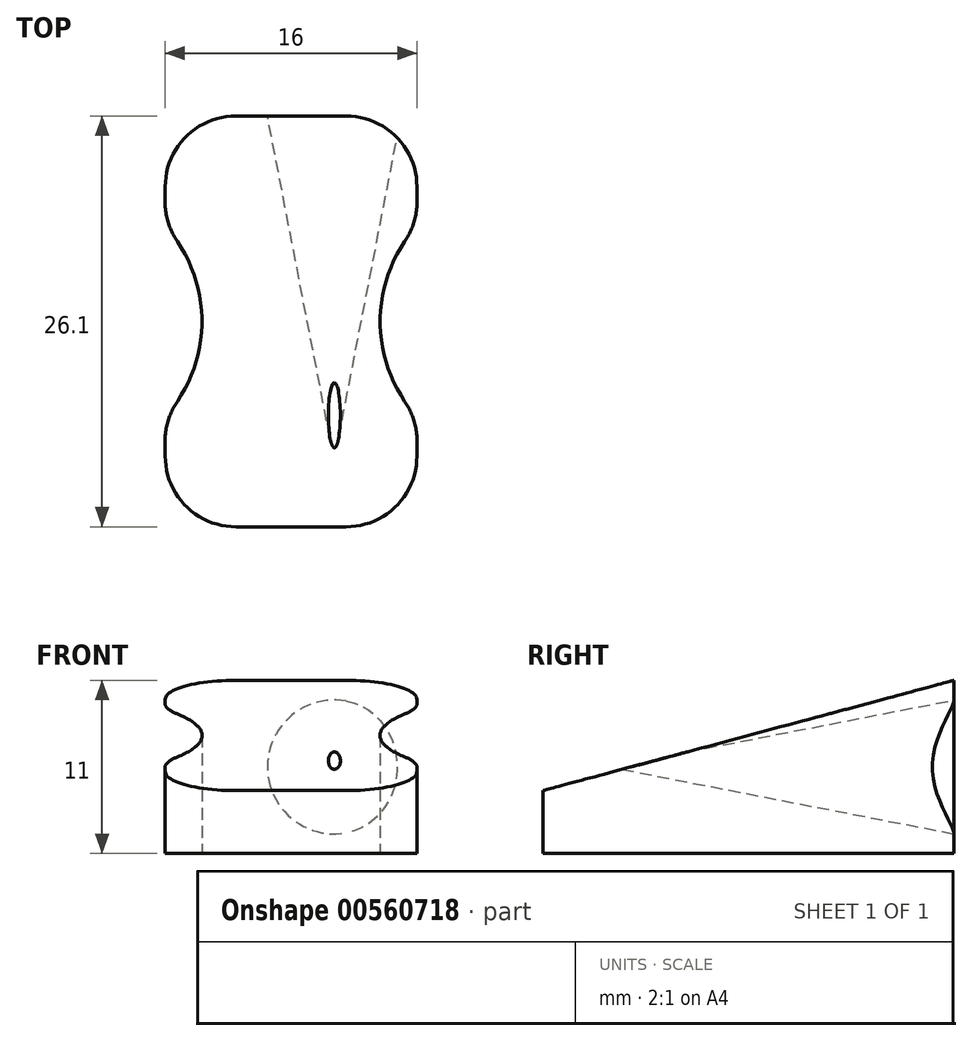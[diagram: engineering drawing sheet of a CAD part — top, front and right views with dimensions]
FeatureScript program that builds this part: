
annotation { "Feature Type Name" : "Feature", "Feature Type Description" : "" }
export const myFeature = defineFeature(function(context is Context, id is Id, definition is map)
    precondition{}
    {
        {
            var Q0;
            Q0=qCreatedBy(makeId("Top.planeOp"),FACE);
            var sketch = newSketch(context, id + "F0", { "sketchPlane" : qUnion([Q0])});
            skLineSegment(sketch, "E0.bottom", {"start": v(-8, 26.1) * mm, "end": v(8, 26.1) * mm});
            skLineSegment(sketch, "E0.top", {"start": v(-8, 0) * mm, "end": v(8, 0) * mm});
            skLineSegment(sketch, "E0.left", {"start": v(-8, 26.1) * mm, "end": v(-8, 0) * mm});
            skLineSegment(sketch, "E0.right", {"start": v(8, 26.1) * mm, "end": v(8, 0) * mm});
            skSolve(sketch);
        }
        {
            var Q0;
            Q0 = qSketchRegion(id + "F0", true);
            extrude(context, id + "F1", {"entities" : qUnion([Q0]), "depth" : 11 * mm, "offsetDistance" : 25 * mm});
        }
        {
            var Q0;
            Q0=qCreatedBy(makeId("Top.planeOp"),FACE);
            var sketch = newSketch(context, id + "F2", { "sketchPlane" : qUnion([Q0])});
            skLineSegment(sketch, "E1", {"start": v(0, 26.1) * mm, "end": v(0, 0) * mm, "construction": true});
            skLineSegment(sketch, "E2", {"start": v(0, 13.05) * mm, "end": v(-14.65, 13.05) * mm, "construction": true});
            skPoint(sketch, "E2.endSnap0", {"position": v(0, 13.05) * mm});
            skCircle(sketch, "E3", {"center": v(-14.65, 13.05) * mm, "radius": 9 * mm});
            skCircle(sketch, "E4.MirrorC", {"center": v(14.65, 13.05) * mm, "radius": 9 * mm});
            skSolve(sketch);
        }
        {
            var Q0;
            Q0 = qSketchRegion(id + "F2", true);
            extrude(context, id + "F3", {"entities" : qUnion([Q0]), "operationType" : NewBodyOperationType.REMOVE, "depth" : 25 * mm, "offsetDistance" : 25 * mm});
        }
        {
            var Q0;
            Q0=qCreatedBy(makeId("Right.planeOp"),FACE);
            var sketch = newSketch(context, id + "F4", { "sketchPlane" : qUnion([Q0])});
            skLineSegment(sketch, "E5", {"start": v(26.1, 11) * mm, "end": v(0, 4) * mm});
            skLineSegment(sketch, "E6", {"start": v(26.1, 11) * mm, "end": v(0, 11) * mm});
            skLineSegment(sketch, "E7", {"start": v(0, 11) * mm, "end": v(0, 4) * mm});
            skSolve(sketch);
        }
        {
            var Q0;
            Q0 = qSketchRegion(id + "F4", true);
            extrude(context, id + "F5", {"entities" : qUnion([Q0]), "operationType" : NewBodyOperationType.REMOVE, "endBound" : BoundingType.SYMMETRIC, "oppositeDirection" : true, "depth" : 25 * mm, "offsetDistance" : 25 * mm});
        }
        {
            var Q0;
            Q0=makeQuery(id+"F1.opExtrude","SWEPT_EDGE",EDGE,{"disambiguationData":[OSD([sQuery(id+"F0.wireOp",EDGE,"E0.bottom"),sQuery(id+"F0.wireOp",EDGE,"E0.left")])]});
            var Q1;
            Q1=makeQuery(id+"F3.boolean.opBoolean","INTERSECT",EDGE,{"disambiguationData":[OD(0.0)],"derivedFrom":[makeQuery(id+"F1.opExtrude","SWEPT_FACE",FACE,{"disambiguationData":[OSD([sQuery(id+"F0.wireOp",EDGE,"E0.left")])]}),makeQuery(id+"F3.opExtrude","SWEPT_FACE",FACE,{"disambiguationData":[OSD([sQuery(id+"F2.wireOp",EDGE,"E3")])]})]});
            var Q2;
            Q2=makeQuery(id+"F1.opExtrude","SWEPT_EDGE",EDGE,{"disambiguationData":[OSD([sQuery(id+"F0.wireOp",EDGE,"E0.top"),sQuery(id+"F0.wireOp",EDGE,"E0.left")])]});
            var Q3;
            Q3=makeQuery(id+"F3.boolean.opBoolean","INTERSECT",EDGE,{"disambiguationData":[OD(1.0)],"derivedFrom":[makeQuery(id+"F1.opExtrude","SWEPT_FACE",FACE,{"disambiguationData":[OSD([sQuery(id+"F0.wireOp",EDGE,"E0.left")])]}),makeQuery(id+"F3.opExtrude","SWEPT_FACE",FACE,{"disambiguationData":[OSD([sQuery(id+"F2.wireOp",EDGE,"E3")])]})]});
            var Q4;
            Q4=makeQuery(id+"F1.opExtrude","SWEPT_EDGE",EDGE,{"disambiguationData":[OSD([sQuery(id+"F0.wireOp",EDGE,"E0.top"),sQuery(id+"F0.wireOp",EDGE,"E0.right")])]});
            var Q5;
            Q5=makeQuery(id+"F3.boolean.opBoolean","INTERSECT",EDGE,{"disambiguationData":[OD(1.0)],"derivedFrom":[makeQuery(id+"F1.opExtrude","SWEPT_FACE",FACE,{"disambiguationData":[OSD([sQuery(id+"F0.wireOp",EDGE,"E0.right")])]}),makeQuery(id+"F3.opExtrude","SWEPT_FACE",FACE,{"disambiguationData":[OSD([sQuery(id+"F2.wireOp",EDGE,"E4.MirrorC")])]})]});
            var Q6;
            Q6=makeQuery(id+"F3.boolean.opBoolean","INTERSECT",EDGE,{"disambiguationData":[OD(0.0)],"derivedFrom":[makeQuery(id+"F1.opExtrude","SWEPT_FACE",FACE,{"disambiguationData":[OSD([sQuery(id+"F0.wireOp",EDGE,"E0.right")])]}),makeQuery(id+"F3.opExtrude","SWEPT_FACE",FACE,{"disambiguationData":[OSD([sQuery(id+"F2.wireOp",EDGE,"E4.MirrorC")])]})]});
            var Q7;
            Q7=makeQuery(id+"F1.opExtrude","SWEPT_EDGE",EDGE,{"disambiguationData":[OSD([sQuery(id+"F0.wireOp",EDGE,"E0.bottom"),sQuery(id+"F0.wireOp",EDGE,"E0.right")])]});
            fillet(context, id + "F6", {"entities" : qUnion([Q0, Q1, Q2, Q3, Q4, Q5, Q6, Q7]), "radius" : 4.5 * mm, "tangentPropagation" : true, "allowEdgeOverflow" : false});
        }
        {
            var Q0;
            Q0=makeQuery(id+"F1.opExtrude","SWEPT_FACE",FACE,{"disambiguationData":[OSD([sQuery(id+"F0.wireOp",EDGE,"E0.bottom")])]});
            var sketch = newSketch(context, id + "F7", { "sketchPlane" : qUnion([Q0])});
            skCircle(sketch, "E8", {"center": v(-2.75, 5.5) * mm, "radius": 4.25 * mm});
            skLineSegment(sketch, "E9", {"start": v(0, 0) * mm, "end": v(0, 11) * mm, "construction": true});
            skLineSegment(sketch, "E10", {"start": v(0, 5.5) * mm, "end": v(-2.75, 5.5) * mm, "construction": true});
            skPoint(sketch, "E10.endSnap0", {"position": v(0, 5.5) * mm});
            skSolve(sketch);
        }
        {
            var Q0;
            Q0 = qSketchRegion(id + "F7", true);
            extrude(context, id + "F8", {"entities" : qUnion([Q0]), "operationType" : NewBodyOperationType.REMOVE, "oppositeDirection" : true, "depth" : 30 * mm, "offsetDistance" : 25 * mm, "hasDraft" : true, "draftAngle" : 11 * degree, "draftPullDirection" : true});
        }
    });
